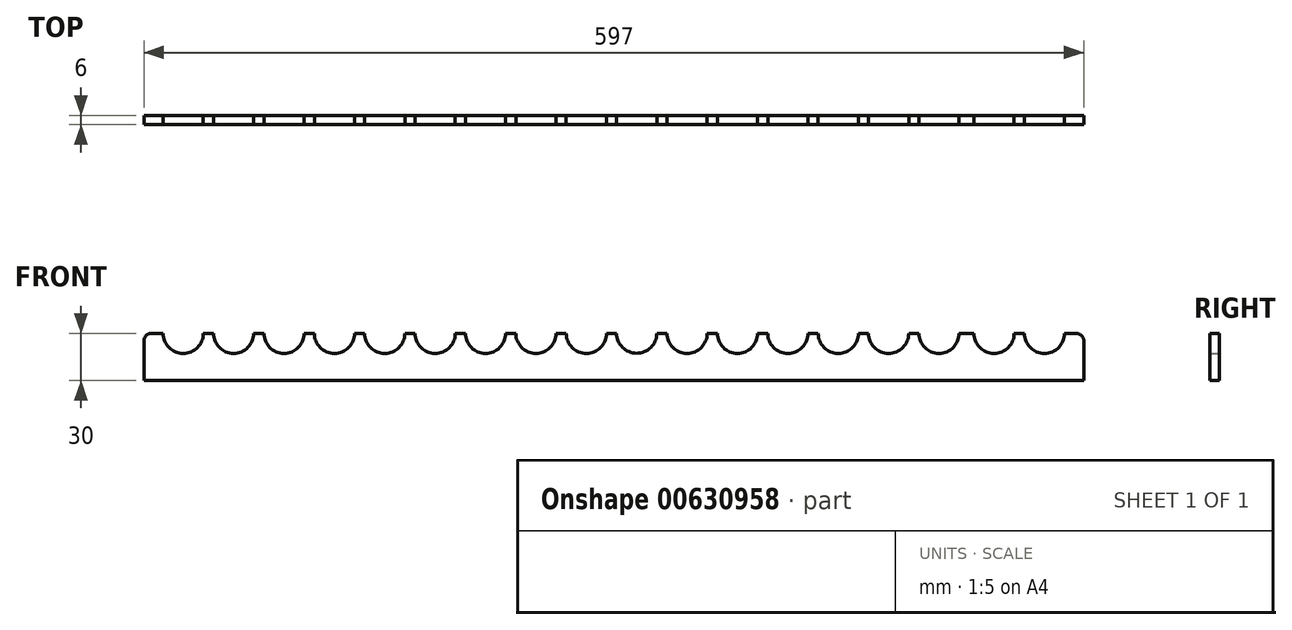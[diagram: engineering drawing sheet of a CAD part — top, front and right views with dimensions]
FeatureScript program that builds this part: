
annotation { "Feature Type Name" : "Feature", "Feature Type Description" : "" }
export const myFeature = defineFeature(function(context is Context, id is Id, definition is map)
    precondition{}
    {
        {
            var Q0;
            Q0=qCreatedBy(makeId("Front.planeOp"),FACE);
            var sketch = newSketch(context, id + "F0", { "sketchPlane" : qUnion([Q0])});
            skLineSegment(sketch, "E0.bottom", {"start": v(298.5, -15) * mm, "end": v(-298.5, -15) * mm});
            skLineSegment(sketch, "E0.top", {"start": v(293.5, 15) * mm, "end": v(286.25, 15) * mm});
            skLineSegment(sketch, "E0.left", {"start": v(298.5, -15) * mm, "end": v(298.5, 10) * mm});
            skLineSegment(sketch, "E0.right", {"start": v(-298.5, -15) * mm, "end": v(-298.5, 10) * mm});
            skPoint(sketch, "E0.middle", {"position": v(0, 0) * mm});
            skLineSegment(sketch, "E1", {"start": v(-273.5, 46.82) * mm, "end": v(-273.5, -38.88) * mm, "construction": true});
            skLineSegment(sketch, "E2", {"start": v(-241.5, 23.66) * mm, "end": v(-241.5, -34.17) * mm, "construction": true});
            skLineSegment(sketch, "E3", {"start": v(-209.5, 23.83) * mm, "end": v(-209.5, -35.98) * mm, "construction": true});
            skLineSegment(sketch, "E4", {"start": v(-177.5, 23.92) * mm, "end": v(-177.5, -34.36) * mm, "construction": true});
            skLineSegment(sketch, "E5", {"start": v(-145.5, 24.14) * mm, "end": v(-145.5, -36) * mm, "construction": true});
            skLineSegment(sketch, "E6", {"start": v(-113.5, 23) * mm, "end": v(-113.5, -28.62) * mm, "construction": true});
            skLineSegment(sketch, "E7", {"start": v(-81.5, 24.21) * mm, "end": v(-81.5, -35.73) * mm, "construction": true});
            skLineSegment(sketch, "E8", {"start": v(-49.5, 20.5) * mm, "end": v(-49.5, -34.07) * mm, "construction": true});
            skLineSegment(sketch, "E9", {"start": v(-17.5, 20.46) * mm, "end": v(-17.5, -36.64) * mm, "construction": true});
            skLineSegment(sketch, "E10", {"start": v(14.5, 15.11) * mm, "end": v(14.5, -43.64) * mm, "construction": true});
            skLineSegment(sketch, "E11", {"start": v(46.5, 36.2) * mm, "end": v(46.5, -51.81) * mm, "construction": true});
            skLineSegment(sketch, "E12", {"start": v(110.5, 31.53) * mm, "end": v(110.5, -51.35) * mm, "construction": true});
            skLineSegment(sketch, "E13", {"start": v(78.5, 20.46) * mm, "end": v(78.5, -47.48) * mm, "construction": true});
            skLineSegment(sketch, "E14", {"start": v(142.5, 30.81) * mm, "end": v(142.5, -46.92) * mm, "construction": true});
            skLineSegment(sketch, "E15", {"start": v(174.5, 33.03) * mm, "end": v(174.5, -57.47) * mm, "construction": true});
            skLineSegment(sketch, "E16", {"start": v(241.5, 36.92) * mm, "end": v(241.5, -63.58) * mm, "construction": true});
            skLineSegment(sketch, "E17", {"start": v(206.5, 42.47) * mm, "end": v(206.5, -60.8) * mm, "construction": true});
            skPoint(sketch, "E18.first.point", {"position": v(-273.5, 15) * mm});
            skPoint(sketch, "E18.second.point", {"position": v(-282.4, 15) * mm});
            skPoint(sketch, "E18.third.point", {"position": v(-273.5, 6.15) * mm});
            skArc(sketch, "E19", {"start": v(-286.25, 15) * mm, "mid": v(-273.5, 2.25) * mm, "end": v(-260.75, 15) * mm});
            skArc(sketch, "E20", {"start": v(-254.25, 15) * mm, "mid": v(-241.5, 2.25) * mm, "end": v(-228.75, 15) * mm});
            skArc(sketch, "E21", {"start": v(-222.25, 15) * mm, "mid": v(-209.5, 2.25) * mm, "end": v(-196.75, 15) * mm});
            skArc(sketch, "E22", {"start": v(-190.25, 15) * mm, "mid": v(-177.5, 2.25) * mm, "end": v(-164.75, 15) * mm});
            skArc(sketch, "E23", {"start": v(-158.25, 15) * mm, "mid": v(-145.5, 2.25) * mm, "end": v(-132.75, 15) * mm});
            skArc(sketch, "E24", {"start": v(-126.25, 15) * mm, "mid": v(-113.5, 2.25) * mm, "end": v(-100.75, 15) * mm});
            skArc(sketch, "E25", {"start": v(-94.25, 15) * mm, "mid": v(-81.5, 2.25) * mm, "end": v(-68.75, 15) * mm});
            skArc(sketch, "E26", {"start": v(-62.25, 15) * mm, "mid": v(-49.5, 2.25) * mm, "end": v(-36.75, 15) * mm});
            skArc(sketch, "E27", {"start": v(-30.25, 15) * mm, "mid": v(-17.5, 2.25) * mm, "end": v(-4.75, 15) * mm});
            skArc(sketch, "E28", {"start": v(1.75, 15) * mm, "mid": v(14.5, 2.36) * mm, "end": v(27.25, 15) * mm});
            skArc(sketch, "E29", {"start": v(33.75, 15) * mm, "mid": v(46.5, 2.25) * mm, "end": v(59.25, 15) * mm});
            skArc(sketch, "E30", {"start": v(65.75, 15) * mm, "mid": v(78.5, 2.25) * mm, "end": v(91.25, 15) * mm});
            skArc(sketch, "E31", {"start": v(161.75, 15) * mm, "mid": v(174.5, 2.25) * mm, "end": v(187.25, 15) * mm});
            skArc(sketch, "E32", {"start": v(228.75, 15) * mm, "mid": v(241.5, 2.25) * mm, "end": v(254.25, 15) * mm});
            skArc(sketch, "E33", {"start": v(193.75, 15) * mm, "mid": v(206.5, 2.25) * mm, "end": v(219.25, 15) * mm});
            skArc(sketch, "E34", {"start": v(97.75, 15) * mm, "mid": v(110.5, 2.25) * mm, "end": v(123.25, 15) * mm});
            skArc(sketch, "E35", {"start": v(129.75, 15) * mm, "mid": v(142.5, 2.25) * mm, "end": v(155.25, 15) * mm});
            skLineSegment(sketch, "E36.trimOffspring", {"start": v(228.75, 15) * mm, "end": v(219.25, 15) * mm});
            skLineSegment(sketch, "E37.trimOffspring", {"start": v(193.75, 15) * mm, "end": v(187.25, 15) * mm});
            skLineSegment(sketch, "E38.trimOffspring", {"start": v(161.75, 15) * mm, "end": v(155.25, 15) * mm});
            skLineSegment(sketch, "E39.trimOffspring", {"start": v(129.75, 15) * mm, "end": v(123.25, 15) * mm});
            skLineSegment(sketch, "E40.trimOffspring", {"start": v(97.75, 15) * mm, "end": v(91.25, 15) * mm});
            skLineSegment(sketch, "E41.trimOffspring", {"start": v(65.75, 15) * mm, "end": v(59.25, 15) * mm});
            skLineSegment(sketch, "E42.trimOffspring", {"start": v(33.75, 15) * mm, "end": v(27.25, 15) * mm});
            skLineSegment(sketch, "E43.trimOffspring", {"start": v(1.75, 15) * mm, "end": v(-4.75, 15) * mm});
            skLineSegment(sketch, "E44.trimOffspring", {"start": v(-30.25, 15) * mm, "end": v(-36.75, 15) * mm});
            skLineSegment(sketch, "E45.trimOffspring", {"start": v(-62.25, 15) * mm, "end": v(-68.75, 15) * mm});
            skLineSegment(sketch, "E46.trimOffspring", {"start": v(-81.5, 15) * mm, "end": v(-100.75, 15) * mm});
            skLineSegment(sketch, "E47.trimOffspring", {"start": v(-126.25, 15) * mm, "end": v(-132.75, 15) * mm});
            skLineSegment(sketch, "E48.trimOffspring", {"start": v(-158.25, 15) * mm, "end": v(-164.75, 15) * mm});
            skLineSegment(sketch, "E49.trimOffspring", {"start": v(-190.25, 15) * mm, "end": v(-196.75, 15) * mm});
            skLineSegment(sketch, "E50.trimOffspring", {"start": v(-222.25, 15) * mm, "end": v(-228.75, 15) * mm});
            skLineSegment(sketch, "E51.trimOffspring", {"start": v(-254.25, 15) * mm, "end": v(-260.75, 15) * mm});
            skArc(sketch, "E52", {"start": v(260.75, 15) * mm, "mid": v(273.5, 2.25) * mm, "end": v(286.25, 15) * mm});
            skLineSegment(sketch, "E53.trimOffspring", {"start": v(260.75, 15) * mm, "end": v(254.25, 15) * mm});
            skLineSegment(sketch, "E54", {"start": v(-286.25, 15) * mm, "end": v(-293.5, 15) * mm});
            skPoint(sketch, "E55.visualSharp", {"position": v(-298.5, 15) * mm});
            skArc(sketch, "E55.filletArc", {"start": v(-293.5, 15) * mm, "mid": v(-297.04, 13.54) * mm, "end": v(-298.5, 10) * mm});
            skPoint(sketch, "E56.visualSharp", {"position": v(298.5, 15) * mm});
            skArc(sketch, "E56.filletArc", {"start": v(298.5, 10) * mm, "mid": v(297.04, 13.54) * mm, "end": v(293.5, 15) * mm});
            skSolve(sketch);
        }
        {
            var Q0;
            Q0 = qSketchRegion(id + "F0", true);
            extrude(context, id + "F1", {"entities" : qUnion([Q0]), "depth" : 6 * mm, "offsetDistance" : 25 * mm});
        }
    });
